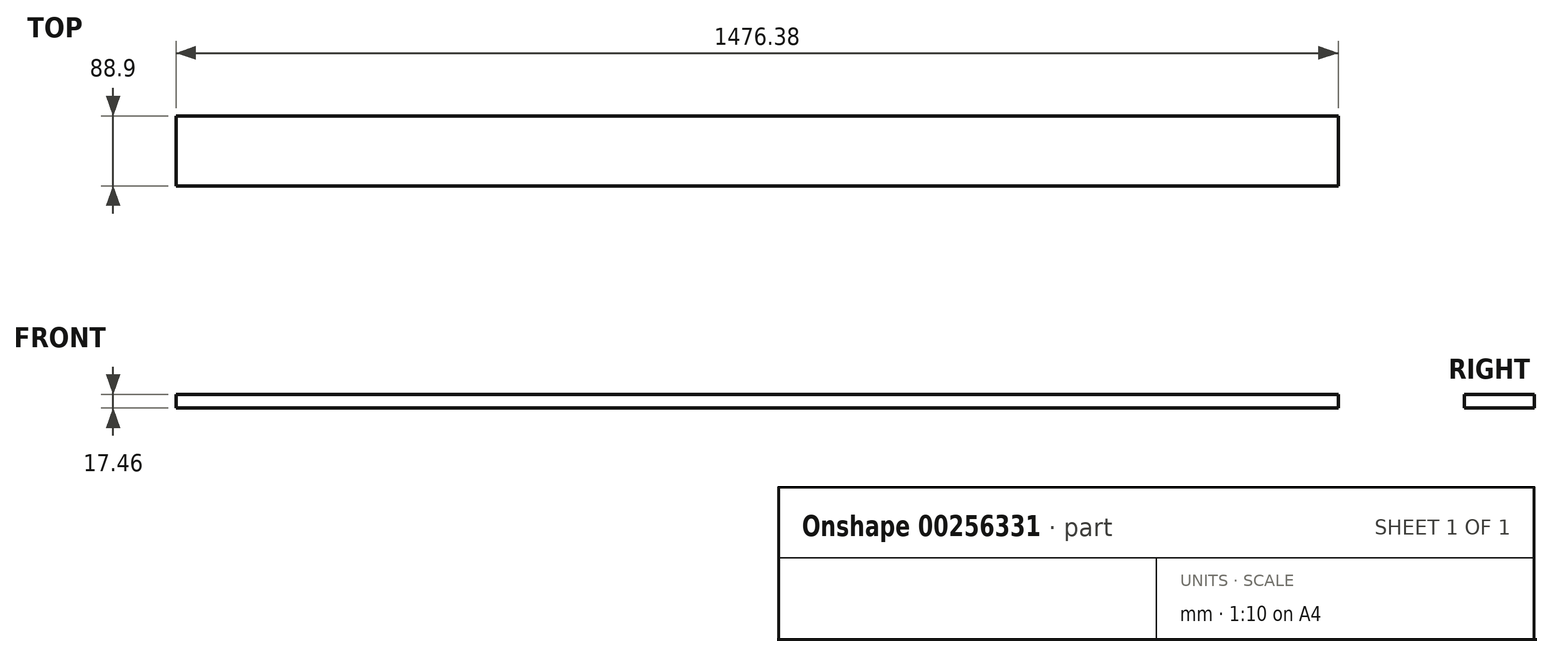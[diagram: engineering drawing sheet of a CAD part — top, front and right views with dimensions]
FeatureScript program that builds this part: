
annotation { "Feature Type Name" : "Feature", "Feature Type Description" : "" }
export const myFeature = defineFeature(function(context is Context, id is Id, definition is map)
    precondition{}
    {
        {
            var Q0;
            Q0=qCreatedBy(makeId("Right.planeOp"),FACE);
            var sketch = newSketch(context, id + "F0", { "sketchPlane" : qUnion([Q0])});
            skLineSegment(sketch, "E0.bottom", {"start": v(-44.45, 8.73) * mm, "end": v(44.45, 8.73) * mm});
            skLineSegment(sketch, "E0.top", {"start": v(-44.45, -8.73) * mm, "end": v(44.45, -8.73) * mm});
            skLineSegment(sketch, "E0.left", {"start": v(-44.45, 8.73) * mm, "end": v(-44.45, -8.73) * mm});
            skLineSegment(sketch, "E0.right", {"start": v(44.45, 8.73) * mm, "end": v(44.45, -8.73) * mm});
            skSolve(sketch);
        }
        {
            var Q0;
            Q0=qSketchRegion(id+"F0",true);
            extrude(context, id + "F1", {"entities" : qUnion([Q0]), "endBound" : BoundingType.SYMMETRIC, "depth" : 1476.38 * mm});
        }
    });
